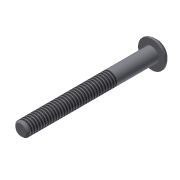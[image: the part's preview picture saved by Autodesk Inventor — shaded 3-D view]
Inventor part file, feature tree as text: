
AUTODESK INVENTOR PART (.ipt)
format: ipt  version: 2013 (Build 170138000, 138)  size: 109,568 bytes
history: native  units: in
note: dims shown in document units (in); Inventor stores cm internally (conversion verified against a paired STEP export)
features: sketch x3, extrude x2, revolve x1, chamfer x1, thread x1
ambient origin geometry x8: Origin, YZ Plane, XZ Plane, XY Plane, X Axis, Y Axis, Z Axis, Center Point
bodies: Solid1 (feature_tree)
feature tree (8):
  extrude  "Extrusion1"  Depth=1.5in TaperAngle=0.0deg
  revolve  "Revolution1"  [1 undecoded]
  extrude  "Extrusion2"  Depth=0.0938in
  chamfer  "Chamfer1"  Distance=0.0625in
  thread  "Thread1"  [1 undecoded]
  sketch  "Sketch1"  dims[d0=0.164in d1=1.5in d2=0.0in]
  sketch  "Sketch2"  dims[d3=0.087in d6=0.08in]
  sketch  "Sketch3"  dims[d7=90.0deg d8=0.0938in d9=0.0625in d10=0.0in d13=0.02in d14=0.125in d15=45.0deg d16=1.0in d17=0.0in d19=0.156in]
note: 2 required parameter values undecoded (feature->parameter linkage not recoverable at this tier; creation-order binding heuristic only, values carry confidence <= 0.55)